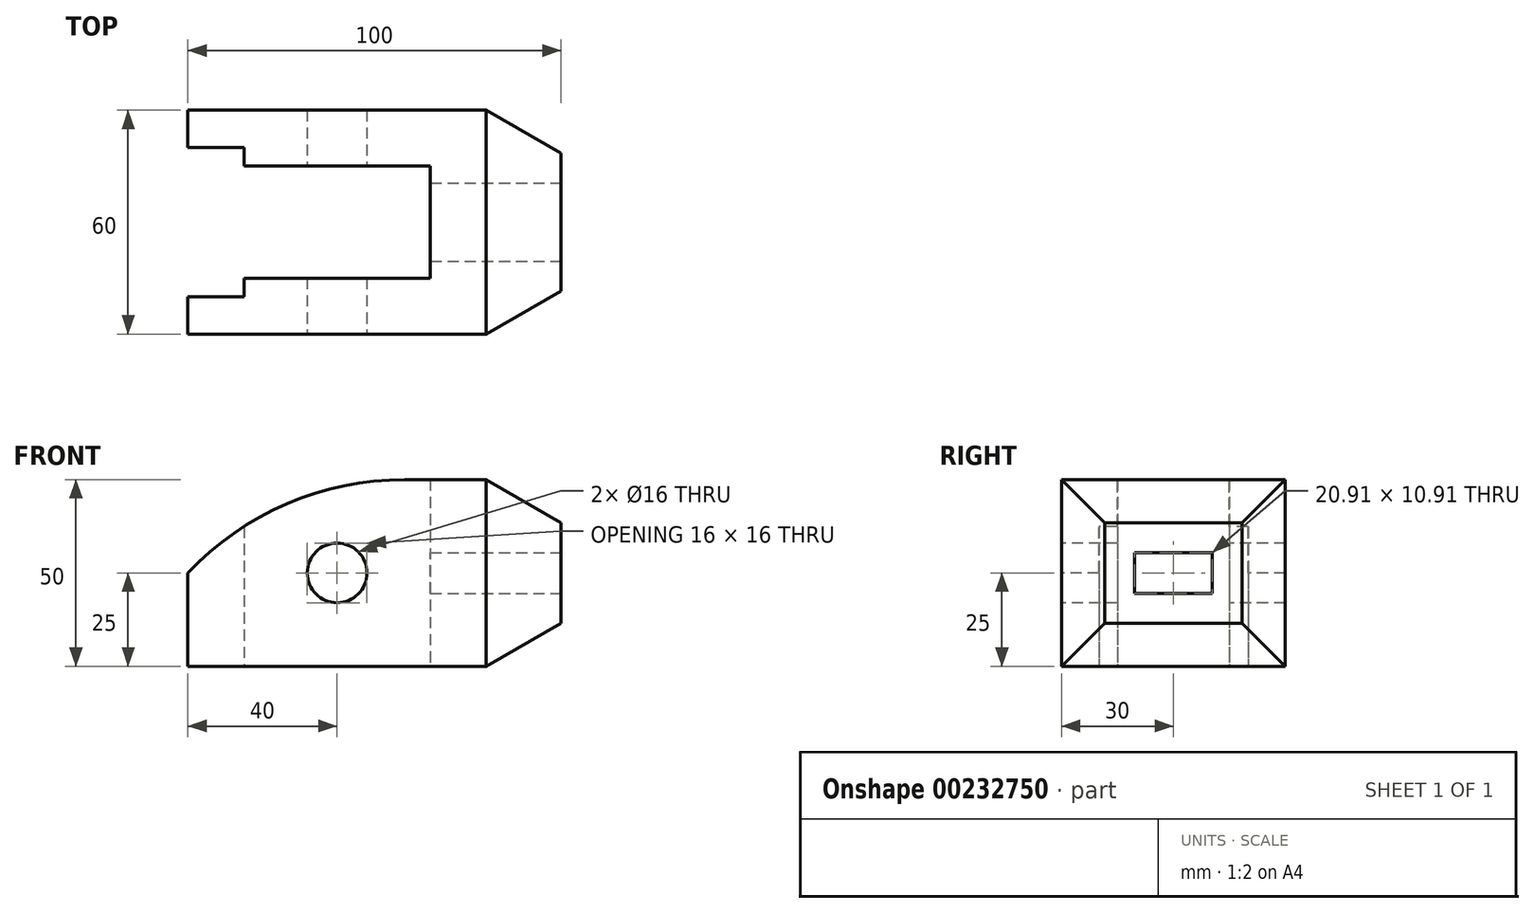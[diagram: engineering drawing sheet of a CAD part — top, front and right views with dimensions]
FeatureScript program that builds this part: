
annotation { "Feature Type Name" : "Feature", "Feature Type Description" : "" }
export const myFeature = defineFeature(function(context is Context, id is Id, definition is map)
    precondition{}
    {
        {
            var Q0;
            Q0=qCreatedBy(makeId("Front.planeOp"),FACE);
            var sketch = newSketch(context, id + "F0", { "sketchPlane" : qUnion([Q0])});
            skLineSegment(sketch, "E0", {"start": v(0, 0) * mm, "end": v(0, 50) * mm});
            skLineSegment(sketch, "E1", {"start": v(0, 50) * mm, "end": v(-21.9, 50) * mm});
            skArc(sketch, "E2", {"start": v(-21.9, 50) * mm, "mid": v(-53.53, 43.48) * mm, "end": v(-80, 25) * mm});
            skLineSegment(sketch, "E3", {"start": v(-80, 25) * mm, "end": v(-80, 0) * mm});
            skLineSegment(sketch, "E4", {"start": v(-80, 0) * mm, "end": v(0, 0) * mm});
            skLineSegment(sketch, "E5", {"start": v(-102.68, 25) * mm, "end": v(17.99, 25) * mm, "construction": true});
            skLineSegment(sketch, "E6", {"start": v(-40, 82.97) * mm, "end": v(-40, 14.25) * mm, "construction": true});
            skCircle(sketch, "E7", {"center": v(-40, 25) * mm, "radius": 8 * mm});
            skSolve(sketch);
        }
        {
            var Q0;
            Q0=makeQuery(id+"F0.imprint","IMPRINT",FACE,{"disambiguationData":[TD([[makeQuery(id+"F0.imprint","IMPRINT",EDGE,{"derivedFrom":sQuery(id+"F0.wireOp",EDGE,"E0")}),1.0]])]});
            extrude(context, id + "F1", {"entities" : qUnion([Q0]), "oppositeDirection" : true, "depth" : 60 * mm});
        }
        {
            var Q0;
            Q0=qCreatedBy(makeId("Top.planeOp"),FACE);
            var sketch = newSketch(context, id + "F2", { "sketchPlane" : qUnion([Q0])});
            skLineSegment(sketch, "E8", {"start": v(-91.07, 30) * mm, "end": v(16.86, 30) * mm, "construction": true});
            skPoint(sketch, "E9", {"position": v(0, 30) * mm});
            skLineSegment(sketch, "E10.0.1", {"start": v(0, 0) * mm, "end": v(0, 60) * mm, "construction": true});
            skLineSegment(sketch, "E11.0.3", {"start": v(-80, 60) * mm, "end": v(-80, 0) * mm, "construction": true});
            skLineSegment(sketch, "E12", {"start": v(-80, 30) * mm, "end": v(-80, 50) * mm});
            skLineSegment(sketch, "E13", {"start": v(-80, 50) * mm, "end": v(-65, 50) * mm});
            skLineSegment(sketch, "E14", {"start": v(-65, 50) * mm, "end": v(-65, 45) * mm});
            skLineSegment(sketch, "E15", {"start": v(-65, 45) * mm, "end": v(-15, 45) * mm});
            skLineSegment(sketch, "E16", {"start": v(-15, 45) * mm, "end": v(-15, 30) * mm});
            skLineSegment(sketch, "E17", {"start": v(-15, 30) * mm, "end": v(-80, 30) * mm});
            skLineSegment(sketch, "E18.MirrorCS", {"start": v(-15, 15) * mm, "end": v(-15, 30) * mm});
            skLineSegment(sketch, "E19.MirrorCS", {"start": v(-65, 15) * mm, "end": v(-15, 15) * mm});
            skLineSegment(sketch, "E20.MirrorCS", {"start": v(-80, 30) * mm, "end": v(-80, 10) * mm});
            skLineSegment(sketch, "E21.MirrorCS", {"start": v(-80, 10) * mm, "end": v(-65, 10) * mm});
            skLineSegment(sketch, "E22.MirrorCS", {"start": v(-65, 10) * mm, "end": v(-65, 15) * mm});
            skSolve(sketch);
        }
        {
            var Q0;
            Q0=makeQuery(id+"F2.imprint","IMPRINT",FACE,{"disambiguationData":[TD([[makeQuery(id+"F2.imprint","IMPRINT",EDGE,{"derivedFrom":sQuery(id+"F2.wireOp",EDGE,"E18.MirrorCS")}),1.0]])]});
            var Q1;
            Q1=makeQuery(id+"F2.imprint","IMPRINT",FACE,{"disambiguationData":[TD([[makeQuery(id+"F2.imprint","IMPRINT",EDGE,{"derivedFrom":sQuery(id+"F2.wireOp",EDGE,"E12")}),-1.0]])]});
            extrude(context, id + "F3", {"entities" : qUnion([Q0, Q1]), "operationType" : NewBodyOperationType.REMOVE, "endBound" : BoundingType.THROUGH_ALL, "depth" : 25 * mm});
        }
        {
            var Q0;
            Q0=qCreatedBy(makeId("Front.planeOp"),FACE);
            var sketch = newSketch(context, id + "F4", { "sketchPlane" : qUnion([Q0])});
            skLineSegment(sketch, "E23", {"start": v(-17.34, -10.04) * mm, "end": v(51, 29.53) * mm, "construction": true});
            skLineSegment(sketch, "E24", {"start": v(0, 0) * mm, "end": v(0, 50) * mm});
            skLineSegment(sketch, "E25", {"start": v(0, 50) * mm, "end": v(20, 50) * mm});
            skLineSegment(sketch, "E26", {"start": v(20, 50) * mm, "end": v(20, 0) * mm});
            skLineSegment(sketch, "E27", {"start": v(20, 0) * mm, "end": v(0, 0) * mm});
            skSolve(sketch);
        }
        {
            var Q0;
            Q0 = qSketchRegion(id + "F4", true);
            extrude(context, id + "F5", {"entities" : qUnion([Q0]), "operationType" : NewBodyOperationType.ADD, "oppositeDirection" : true, "depth" : 60 * mm});
        }
        {
            var Q0;
            Q0=qCreatedBy(makeId("Front.planeOp"),FACE);
            var sketch = newSketch(context, id + "F6", { "sketchPlane" : qUnion([Q0])});
            skLineSegment(sketch, "E28", {"start": v(0, 0) * mm, "end": v(52.34, 30.22) * mm, "construction": true});
            skPoint(sketch, "E29", {"position": v(20, 25) * mm});
            skLineSegment(sketch, "E30", {"start": v(0, 25) * mm, "end": v(61.6, 25) * mm, "construction": true});
            skLineSegment(sketch, "E31", {"start": v(0, 0) * mm, "end": v(20, 11.55) * mm});
            skLineSegment(sketch, "E32", {"start": v(20, 11.55) * mm, "end": v(20, 0) * mm});
            skLineSegment(sketch, "E33", {"start": v(20, 0) * mm, "end": v(0, 0) * mm});
            skLineSegment(sketch, "E34.MirrorCS", {"start": v(0, 50) * mm, "end": v(52.34, 19.78) * mm, "construction": true});
            skLineSegment(sketch, "E35", {"start": v(0, 50) * mm, "end": v(20, 38.45) * mm});
            skLineSegment(sketch, "E36", {"start": v(20, 38.45) * mm, "end": v(20, 50) * mm});
            skLineSegment(sketch, "E37", {"start": v(20, 50) * mm, "end": v(0, 50) * mm});
            skSolve(sketch);
        }
        {
            var Q0;
            Q0=makeQuery(id+"F6.imprint","IMPRINT",FACE,{"disambiguationData":[TD([[makeQuery(id+"F6.imprint","IMPRINT",EDGE,{"derivedFrom":sQuery(id+"F6.wireOp",EDGE,"E35")}),1.0]])]});
            var Q1;
            Q1=makeQuery(id+"F6.imprint","IMPRINT",FACE,{"disambiguationData":[TD([[makeQuery(id+"F6.imprint","IMPRINT",EDGE,{"derivedFrom":sQuery(id+"F6.wireOp",EDGE,"E31")}),-1.0]])]});
            extrude(context, id + "F7", {"entities" : qUnion([Q0, Q1]), "operationType" : NewBodyOperationType.REMOVE, "endBound" : BoundingType.THROUGH_ALL, "oppositeDirection" : true, "depth" : 25 * mm});
        }
        {
            var Q0;
            Q0=makeQuery(id+"F5.boolean.opBoolean","MERGE",FACE,{"derivedFrom":[makeQuery(id+"F1.opExtrude","SWEPT_FACE",FACE,{"disambiguationData":[OSD([sQuery(id+"F0.wireOp",EDGE,"E1")])]}),makeQuery(id+"F5.opExtrude","SWEPT_FACE",FACE,{"disambiguationData":[OSD([sQuery(id+"F4.wireOp",EDGE,"E25")])]})]});
            var sketch = newSketch(context, id + "F8", { "sketchPlane" : qUnion([Q0])});
            skLineSegment(sketch, "E38", {"start": v(0, 60) * mm, "end": v(47.62, 32.5) * mm, "construction": true});
            skLineSegment(sketch, "E39", {"start": v(0, 60) * mm, "end": v(48.68, 60) * mm, "construction": true});
            skLineSegment(sketch, "E40", {"start": v(0, 30) * mm, "end": v(69.18, 30) * mm, "construction": true});
            skLineSegment(sketch, "E41", {"start": v(0, 60) * mm, "end": v(20, 60) * mm});
            skLineSegment(sketch, "E42", {"start": v(20, 60) * mm, "end": v(20, 48.45) * mm});
            skLineSegment(sketch, "E43", {"start": v(20, 48.45) * mm, "end": v(0, 60) * mm});
            skLineSegment(sketch, "E44.MirrorCS", {"start": v(0, 0) * mm, "end": v(47.62, 27.5) * mm, "construction": true});
            skLineSegment(sketch, "E45", {"start": v(0, 0) * mm, "end": v(20, 0) * mm});
            skLineSegment(sketch, "E46", {"start": v(20, 0) * mm, "end": v(20, 11.55) * mm});
            skLineSegment(sketch, "E47", {"start": v(20, 11.55) * mm, "end": v(0, 0) * mm});
            skSolve(sketch);
        }
        {
            var Q0;
            Q0=makeQuery(id+"F8.imprint","IMPRINT",FACE,{"disambiguationData":[TD([[makeQuery(id+"F8.imprint","IMPRINT",EDGE,{"derivedFrom":sQuery(id+"F8.wireOp",EDGE,"E45")}),1.0]])]});
            var Q1;
            Q1=makeQuery(id+"F8.imprint","IMPRINT",FACE,{"disambiguationData":[TD([[makeQuery(id+"F8.imprint","IMPRINT",EDGE,{"derivedFrom":sQuery(id+"F8.wireOp",EDGE,"E41")}),-1.0]])]});
            extrude(context, id + "F9", {"entities" : qUnion([Q0, Q1]), "operationType" : NewBodyOperationType.REMOVE, "endBound" : BoundingType.THROUGH_ALL, "oppositeDirection" : true, "depth" : 25 * mm});
        }
        {
            var Q0;
            Q0=qCreatedBy(makeId("Top.planeOp"),FACE);
            var sketch = newSketch(context, id + "F10", { "sketchPlane" : qUnion([Q0])});
            skLineSegment(sketch, "E48", {"start": v(0, 0) * mm, "end": v(20, 11.55) * mm});
            skLineSegment(sketch, "E49", {"start": v(0, 0) * mm, "end": v(20, 0) * mm});
            skLineSegment(sketch, "E50", {"start": v(20, 0) * mm, "end": v(20, 11.55) * mm});
            skLineSegment(sketch, "E51.MirrorCS", {"start": v(0, 60) * mm, "end": v(20, 60) * mm});
            skLineSegment(sketch, "E52.MirrorCS", {"start": v(0, 60) * mm, "end": v(20, 48.45) * mm});
            skLineSegment(sketch, "E53.MirrorCS", {"start": v(20, 60) * mm, "end": v(20, 48.45) * mm});
            skSolve(sketch);
        }
        {
            var Q0;
            Q0=makeQuery(id+"F10.imprint","IMPRINT",FACE,{"disambiguationData":[TD([[makeQuery(id+"F10.imprint","IMPRINT",EDGE,{"derivedFrom":sQuery(id+"F10.wireOp",EDGE,"E48")}),-1.0]])]});
            var Q1;
            Q1=makeQuery(id+"F10.imprint","IMPRINT",FACE,{"disambiguationData":[TD([[makeQuery(id+"F10.imprint","IMPRINT",EDGE,{"derivedFrom":sQuery(id+"F10.wireOp",EDGE,"E51.MirrorCS")}),-1.0]])]});
            extrude(context, id + "F13", {"entities" : qUnion([Q0, Q1]), "operationType" : NewBodyOperationType.REMOVE, "endBound" : BoundingType.THROUGH_ALL, "depth" : 25 * mm});
        }
        {
            var Q0;
            Q0=makeQuery(id+"F5.opExtrude","SWEPT_FACE",FACE,{"disambiguationData":[OSD([sQuery(id+"F4.wireOp",EDGE,"E26")])]});
            var sketch = newSketch(context, id + "F11", { "sketchPlane" : qUnion([Q0])});
            skLineSegment(sketch, "E54.bottom", {"start": v(19.55, 30.45) * mm, "end": v(40.45, 30.45) * mm});
            skLineSegment(sketch, "E54.top", {"start": v(19.55, 19.55) * mm, "end": v(40.45, 19.55) * mm});
            skLineSegment(sketch, "E54.left", {"start": v(19.55, 30.45) * mm, "end": v(19.55, 19.55) * mm});
            skLineSegment(sketch, "E54.right", {"start": v(40.45, 30.45) * mm, "end": v(40.45, 19.55) * mm});
            skSolve(sketch);
        }
        {
            var Q0;
            Q0=makeQuery(id+"F11.imprint","IMPRINT",FACE,{"disambiguationData":[TD([[makeQuery(id+"F11.imprint","IMPRINT",EDGE,{"derivedFrom":sQuery(id+"F11.wireOp",EDGE,"E54.bottom")}),-1.0]])]});
            extrude(context, id + "F12", {"entities" : qUnion([Q0]), "operationType" : NewBodyOperationType.REMOVE, "endBound" : BoundingType.THROUGH_ALL, "oppositeDirection" : true, "depth" : 25 * mm});
        }
    });
